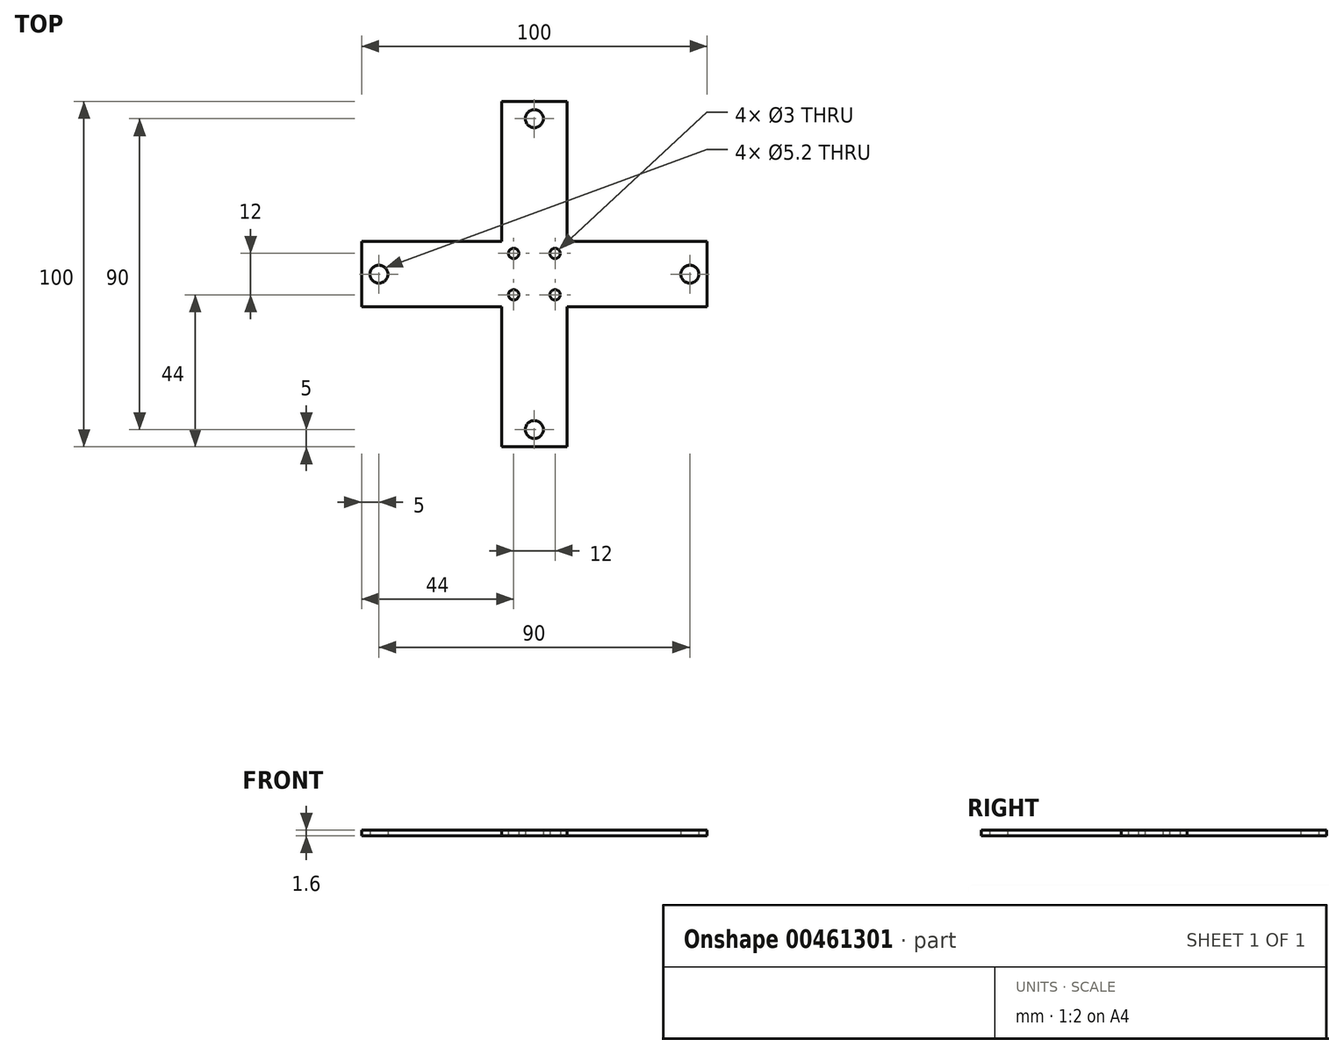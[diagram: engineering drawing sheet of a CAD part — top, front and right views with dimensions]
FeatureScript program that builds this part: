
annotation { "Feature Type Name" : "Feature", "Feature Type Description" : "" }
export const myFeature = defineFeature(function(context is Context, id is Id, definition is map)
    precondition{}
    {
        {
            var Q0;
            Q0=qCreatedBy(makeId("Top.planeOp"),FACE);
            var sketch = newSketch(context, id + "F0", { "sketchPlane" : qUnion([Q0])});
            skLineSegment(sketch, "E0", {"start": v(-9.5, 50) * mm, "end": v(9.5, 50) * mm});
            skLineSegment(sketch, "E1", {"start": v(9.5, 50) * mm, "end": v(9.5, 9.5) * mm});
            skLineSegment(sketch, "E2", {"start": v(9.5, 9.5) * mm, "end": v(50, 9.5) * mm});
            skLineSegment(sketch, "E3", {"start": v(50, 9.5) * mm, "end": v(50, -9.5) * mm});
            skLineSegment(sketch, "E4", {"start": v(50, -9.5) * mm, "end": v(9.5, -9.5) * mm});
            skLineSegment(sketch, "E5", {"start": v(9.5, -9.5) * mm, "end": v(9.5, -50) * mm});
            skLineSegment(sketch, "E6", {"start": v(9.5, -50) * mm, "end": v(-9.5, -50) * mm});
            skLineSegment(sketch, "E7", {"start": v(-9.5, -50) * mm, "end": v(-9.5, -9.5) * mm});
            skLineSegment(sketch, "E8", {"start": v(-9.5, -9.5) * mm, "end": v(-50, -9.5) * mm});
            skLineSegment(sketch, "E9", {"start": v(-50, -9.5) * mm, "end": v(-50, 9.5) * mm});
            skLineSegment(sketch, "E10", {"start": v(-50, 9.5) * mm, "end": v(-9.5, 9.5) * mm});
            skLineSegment(sketch, "E11", {"start": v(-9.5, 9.5) * mm, "end": v(-9.5, 50) * mm});
            skCircle(sketch, "E12", {"center": v(0, 45) * mm, "radius": 2.6 * mm});
            skLineSegment(sketch, "E13", {"start": v(0, 103.68) * mm, "end": v(0, -13.68) * mm, "construction": true});
            skPoint(sketch, "E13.endSnap0", {"position": v(0, -50) * mm});
            skLineSegment(sketch, "E14", {"start": v(-57.87, 0) * mm, "end": v(56.03, 0) * mm, "construction": true});
            skCircle(sketch, "E15.1.0", {"center": v(45, 0) * mm, "radius": 2.6 * mm});
            skCircle(sketch, "E15.2.0", {"center": v(0, -45) * mm, "radius": 2.6 * mm});
            skCircle(sketch, "E15.3.0", {"center": v(-45, 0) * mm, "radius": 2.6 * mm});
            skPoint(sketch, "E15.center", {"position": v(0, 0) * mm});
            skLineSegment(sketch, "E15.anchor1", {"start": v(0, 0) * mm, "end": v(0, 45) * mm, "construction": true});
            skLineSegment(sketch, "E15.anchor2", {"start": v(0, 0) * mm, "end": v(-45, 0) * mm, "construction": true});
            skCircle(sketch, "E16", {"center": v(6, 6) * mm, "radius": 1.5 * mm});
            skCircle(sketch, "E17.1.0", {"center": v(-6, 6) * mm, "radius": 1.5 * mm});
            skCircle(sketch, "E17.2.0", {"center": v(-6, -6) * mm, "radius": 1.5 * mm});
            skCircle(sketch, "E17.3.0", {"center": v(6, -6) * mm, "radius": 1.5 * mm});
            skSolve(sketch);
        }
        {
            var Q0;
            Q0 = qSketchRegion(id + "F0", true);
            extrude(context, id + "F1", {"entities" : qUnion([Q0]), "depth" : 1.6 * mm});
        }
    });
